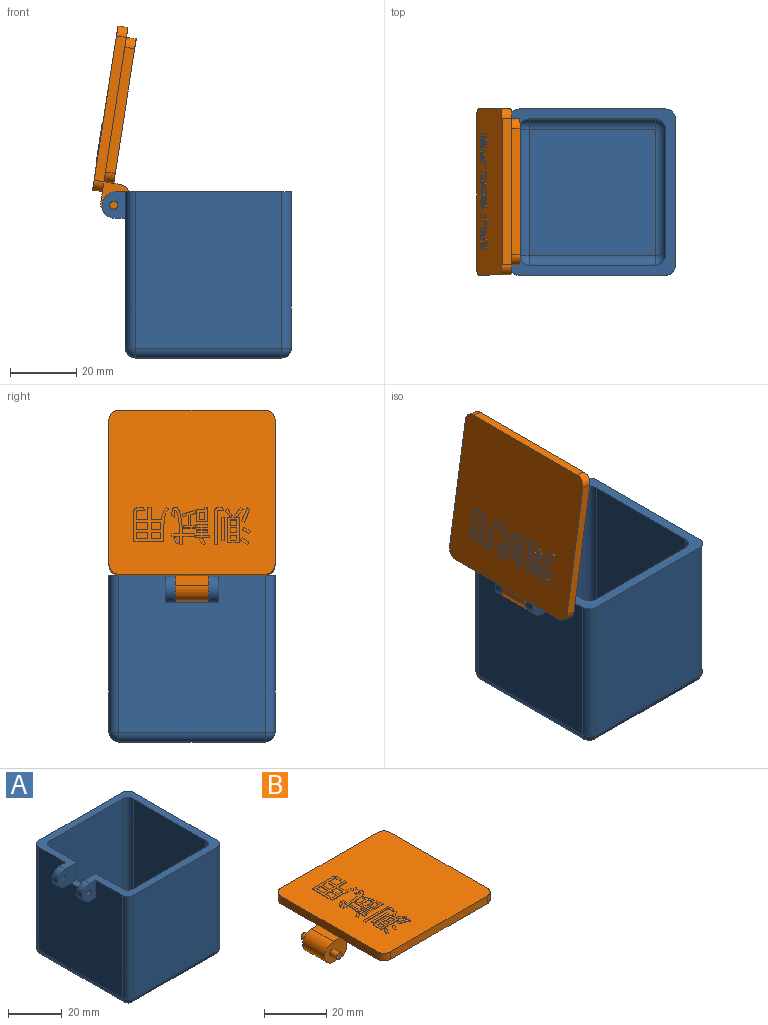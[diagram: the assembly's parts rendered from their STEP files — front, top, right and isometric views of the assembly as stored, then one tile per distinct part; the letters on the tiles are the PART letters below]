
ASSEMBLY  parts=2 mates=1
PART A: 46 faces, bbox 57x50x50 mm
  f0: plane 47x44mm, normal (-1,0,0), area 1940mm2, adj f1,f13,f14,f15,f16,f17,f34,f36
  f1: plane 53x50mm, normal (0,0,1), area 552mm2, adj f0,f2,f3,f4,f5,f7,f8,f9
  f2: plane 44x38mm, normal (1,0,0), area 1592mm2, adj f1,f11,f12,f13,f22,f26,f27
  f3: plane 47x44mm, normal (1,0,0), area 2068mm2, adj f1,f39,f43,f45
  f4: plane 47x44mm, normal (0,1,0), area 2068mm2, adj f1,f36,f42,f45
  f5: plane 47x44mm, normal (0,-1,0), area 2068mm2, adj f1,f34,f38,f39
  f6: plane 44x44mm, normal (0,0,-1), area 1936mm2, adj f37,f38,f42,f43
  f7: plane 44x38mm, normal (-1,0,0), area 1672mm2, adj f1,f24,f30,f33
  f8: plane 44x38mm, normal (0,-1,0), area 1672mm2, adj f1,f27,f31,f33
  f9: plane 44x38mm, normal (0,1,0), area 1672mm2, adj f1,f22,f24,f25
  f10: plane 38x38mm, normal (0,0,1), area 1444mm2, adj f25,f26,f30,f31
  f11: plane 10x8mm, normal (0,-1,0), area 68.2mm2, adj f1,f2,f13,f15,f19,f21
  f12: plane 10x8mm, normal (0,1,0), area 68.2mm2, adj f1,f2,f13,f17,f18,f20
  f13: plane 10x3mm, normal (0,0,1), area 30mm2, adj f0,f2,f11,f12
  f14: plane 8x7mm, normal (0,1,0), area 44.2mm2, adj f0,f1,f15,f19,f21
  f15: plane 3x3mm, normal (0,0,-1), area 9mm2, adj f0,f11,f14,f21
  f16: plane 8x7mm, normal (0,-1,0), area 44.2mm2, adj f0,f1,f17,f18,f20
  f17: plane 3x3mm, normal (0,0,-1), area 9mm2, adj f0,f12,f16,f20
  f18: cylinder r=1.25mm len=3mm, axis (0,-1,0), area 23.6mm2, adj f12,f16
  f19: cylinder r=1.25mm len=3mm, axis (0,-1,0), area 23.6mm2, adj f11,f14
  f20: cylinder r=4mm len=8mm, axis (0,1,0), area 37.7mm2, adj f1,f12,f16,f17
  f21: cylinder r=4mm len=8mm, axis (0,1,0), area 37.7mm2, adj f1,f11,f14,f15
  f22: cylinder r=3mm len=44mm, axis (0,0,1), area 207.3mm2, adj f1,f2,f9,f23
  f23: sphere r=3mm, area 14.1mm2, adj f22,f25,f26
  f24: cylinder r=3mm len=44mm, axis (0,0,-1), area 207.3mm2, adj f1,f7,f9,f28
  f25: cylinder r=3mm len=38mm, axis (1,0,0), area 179.1mm2, adj f9,f10,f23,f28
  f26: cylinder r=3mm len=38mm, axis (0,-1,0), area 179.1mm2, adj f2,f10,f23,f29
  f27: cylinder r=3mm len=44mm, axis (0,0,-1), area 207.3mm2, adj f1,f2,f8,f29
  f28: sphere r=3mm, area 14.1mm2, adj f24,f25,f30
  f29: sphere r=3mm, area 14.1mm2, adj f26,f27,f31
  f30: cylinder r=3mm len=38mm, axis (0,1,0), area 179.1mm2, adj f7,f10,f28,f32
  f31: cylinder r=3mm len=38mm, axis (-1,0,0), area 179.1mm2, adj f8,f10,f29,f32
  f32: sphere r=3mm, area 14.1mm2, adj f30,f31,f33
  f33: cylinder r=3mm len=44mm, axis (0,0,1), area 207.3mm2, adj f1,f7,f8,f32
  f34: cylinder r=3mm len=47mm, axis (0,0,1), area 221.5mm2, adj f0,f1,f5,f35
  f35: sphere r=3mm, area 14.1mm2, adj f34,f37,f38
  f36: cylinder r=3mm len=47mm, axis (0,0,-1), area 221.5mm2, adj f0,f1,f4,f40
  f37: cylinder r=3mm len=44mm, axis (0,-1,0), area 207.3mm2, adj f0,f6,f35,f40
  f38: cylinder r=3mm len=44mm, axis (1,0,0), area 207.3mm2, adj f5,f6,f35,f41
  f39: cylinder r=3mm len=47mm, axis (0,0,-1), area 221.5mm2, adj f1,f3,f5,f41
  f40: sphere r=3mm, area 14.1mm2, adj f36,f37,f42
  f41: sphere r=3mm, area 14.1mm2, adj f38,f39,f43
  f42: cylinder r=3mm len=44mm, axis (-1,0,0), area 207.3mm2, adj f4,f6,f40,f44
  f43: cylinder r=3mm len=44mm, axis (0,1,0), area 207.3mm2, adj f3,f6,f41,f44
  f44: sphere r=3mm, area 14.1mm2, adj f42,f43,f45
  f45: cylinder r=3mm len=47mm, axis (0,0,1), area 221.5mm2, adj f1,f3,f4,f44
PART B: 194 faces, bbox 57x50x11.2 mm
  f0: plane 50x50mm, normal (0,0,1), area 2315.2mm2, adj f2,f3,f4,f5,f27,f28,f29,f30
  f1: plane 14x3mm, normal (-1,0,0), area 42mm2, adj f6,f11,f13,f24
  f2: plane 44x3mm, normal (1,0,0), area 132mm2, adj f0,f6,f27,f30
  f3: plane 44x3mm, normal (0,1,0), area 132mm2, adj f0,f6,f27,f28
  f4: plane 44x3mm, normal (-1,0,0), area 132mm2, adj f0,f6,f16,f28,f29
  f5: plane 44x3mm, normal (0,-1,0), area 132mm2, adj f0,f6,f29,f30
  f6: plane 50x50mm, normal (0,0,-1), area 534mm2, adj f1,f2,f3,f4,f5,f7,f8,f9
  f7: plane 38x3mm, normal (1,0,0), area 114mm2, adj f6,f11,f23,f26
  f8: plane 38x3mm, normal (0,-1,0), area 114mm2, adj f6,f11,f23,f24
  f9: plane 14x3mm, normal (-1,0,0), area 42mm2, adj f6,f11,f14,f25
  f10: plane 38x3mm, normal (0,1,0), area 114mm2, adj f6,f11,f25,f26
  f11: plane 44x44mm, normal (0,0,-1), area 1928.3mm2, adj f1,f7,f8,f9,f10,f12,f23,f24
  f12: plane 10x2mm, normal (1,0,0), area 20mm2, adj f11,f13,f14,f22
  f13: plane 10x8mm, normal (0,-1,0), area 66.7mm2, adj f1,f6,f12,f15,f16,f17,f21,f22
  f14: plane 10x8mm, normal (0,1,0), area 66.7mm2, adj f6,f9,f12,f15,f16,f19,f21,f22
  f15: plane 10x3mm, normal (0,0,-1), area 30mm2, adj f13,f14,f21,f22
  f16: plane 10x3mm, normal (0,0,1), area 30mm2, adj f4,f13,f14,f21
  f17: cylinder r=1.2mm len=3mm, axis (0,1,0), area 22.6mm2, adj f13,f18
  f18: plane 2.4x2.4mm, normal (0,-1,0), area 4.5mm2, adj f17
  f19: cylinder r=1.2mm len=3mm, axis (0,-1,0), area 22.6mm2, adj f14,f20
  f20: plane 2.4x2.4mm, normal (0,1,0), area 4.5mm2, adj f19
  f21: cylinder r=4mm len=10mm, axis (0,-1,0), area 125.7mm2, adj f13,f14,f15,f16
  f22: cylinder r=3mm len=10mm, axis (0,1,0), area 47.1mm2, adj f12,f13,f14,f15
  f23: cylinder r=3mm len=3mm, axis (0,0,-1), area 14.1mm2, adj f6,f7,f8,f11
  f24: cylinder r=3mm len=3mm, axis (0,0,1), area 14.1mm2, adj f1,f6,f8,f11
  f25: cylinder r=3mm len=3mm, axis (0,0,-1), area 14.1mm2, adj f6,f9,f10,f11
  f26: cylinder r=3mm len=3mm, axis (0,0,1), area 14.1mm2, adj f6,f7,f10,f11
  f27: cylinder r=3mm len=3mm, axis (0,0,-1), area 14.1mm2, adj f0,f2,f3,f6
  f28: cylinder r=3mm len=3mm, axis (0,0,1), area 14.1mm2, adj f0,f3,f4,f6
  f29: cylinder r=3mm len=3mm, axis (0,0,-1), area 14.1mm2, adj f0,f4,f5,f6
  f30: cylinder r=3mm len=3mm, axis (0,0,1), area 14.1mm2, adj f0,f2,f5,f6
  f31: plane 1.52x0.2mm, normal (0,1,0), area 0.3mm2, adj f32,f46,f47,f48
  f32: plane 1.95x0.2mm, normal (1,0,0), area 0.4mm2, adj f31,f33,f47,f48
  f33: plane 1.52x0.2mm, normal (0,-1,0), area 0.3mm2, adj f32,f46,f47,f48
  f34: plane 1.55x0.2mm, normal (0,1,0), area 0.3mm2, adj f35,f43,f47,f49
  f35: plane 1.95x0.2mm, normal (1,0,0), area 0.4mm2, adj f34,f36,f47,f49
  f36: plane 1.55x0.2mm, normal (0,-1,0), area 0.3mm2, adj f35,f43,f47,f49
  f37: plane 1.51x0.2mm, normal (0,1,0), area 0.3mm2, adj f38,f44,f47,f50
  f38: plane 1.95x0.2mm, normal (1,0,0), area 0.4mm2, adj f37,f39,f47,f50
  f39: plane 1.51x0.2mm, normal (0,-1,0), area 0.3mm2, adj f38,f44,f47,f50
  f40: plane 3.57x0.2mm, normal (-1,0,0), area 0.7mm2, adj f0,f41,f45,f47
  f41: plane 7.73x0.2mm, normal (0,-1,0), area 1.5mm2, adj f0,f40,f42,f47
  f42: plane 3.57x0.2mm, normal (1,0,0), area 0.7mm2, adj f0,f41,f45,f47
  f43: plane 1.95x0.2mm, normal (-1,0,0), area 0.4mm2, adj f34,f36,f47,f49
  f44: plane 1.95x0.2mm, normal (-1,0,0), area 0.4mm2, adj f37,f39,f47,f50
  f45: plane 7.73x0.2mm, normal (0,1,0), area 1.5mm2, adj f0,f40,f42,f47
  f46: plane 1.95x0.2mm, normal (-1,0,0), area 0.4mm2, adj f31,f33,f47,f48
  f47: plane 7.73x3.57mm, normal (0,0,1), area 18.7mm2, adj f31,f32,f33,f34,f35,f36,f37,f38
  f48: plane 1.95x1.52mm, normal (0,0,1), area 3mm2, adj f31,f32,f33,f46
  f49: plane 1.95x1.55mm, normal (0,0,1), area 3mm2, adj f34,f35,f36,f43
  f50: plane 1.95x1.51mm, normal (0,0,1), area 2.9mm2, adj f37,f38,f39,f44
  f51: plane 0.69x0.38mm, normal (-0.87,-0.49,0), area 0.2mm2, adj f0,f52,f54,f55
  f52: extruded ~1.97x1.37mm, area 0.5mm2, adj f0,f51,f53,f55
  f53: plane 0.73x0.46mm, normal (0.85,0.53,0), area 0.2mm2, adj f0,f52,f54,f55
  f54: extruded ~1.89x1.41mm, area 0.5mm2, adj f0,f51,f53,f55
  f55: plane 2.35x2.1mm, normal (0,0,1), area 2mm2, adj f51,f52,f53,f54
  f56: plane 0.85x0.22mm, normal (-0.97,0.25,0), area 0.2mm2, adj f0,f57,f59,f60
  f57: extruded ~2.27x1.64mm, area 0.6mm2, adj f0,f56,f58,f60
  f58: extruded ~0.72x0.51mm, area 0.2mm2, adj f0,f57,f59,f60
  f59: extruded ~2.56x1.78mm, area 0.6mm2, adj f0,f56,f58,f60
  f60: plane 2.78x2.5mm, normal (0,0,1), area 2.5mm2, adj f56,f57,f58,f59
  f61: plane 0.83x0.2mm, normal (-1,0,0), area 0.2mm2, adj f0,f62,f68,f69
  f62: plane 10.14x0.2mm, normal (0,-1,0), area 2mm2, adj f0,f61,f63,f69
  f63: extruded ~0.3x0.27mm, area 0.1mm2, adj f0,f62,f64,f69
  f64: extruded ~1.57x0.2mm, area 0.3mm2, adj f0,f63,f65,f69
  f65: extruded ~0.87x0.27mm, area 0.2mm2, adj f0,f64,f66,f69
  f66: extruded ~1.94x0.2mm, area 0.4mm2, adj f0,f65,f67,f69
  f67: extruded ~0.98x0.48mm, area 0.2mm2, adj f0,f66,f68,f69
  f68: plane 10.13x0.2mm, normal (0,1,0), area 2mm2, adj f0,f61,f67,f69
  f69: plane 11.28x2.7mm, normal (0,0,1), area 10.6mm2, adj f61,f62,f63,f64,f65,f66,f67,f68
  f70: plane 0.82x0.2mm, normal (-1,0,0), area 0.2mm2, adj f0,f71,f73,f74
  f71: plane 7.03x0.2mm, normal (0,-1,0), area 1.4mm2, adj f0,f70,f72,f74
  f72: plane 0.82x0.2mm, normal (1,0,0), area 0.2mm2, adj f0,f71,f73,f74
  f73: plane 7.03x0.2mm, normal (0,1,0), area 1.4mm2, adj f0,f70,f72,f74
  f74: plane 7.03x0.82mm, normal (0,0,1), area 5.7mm2, adj f70,f71,f72,f73
  f75: plane 0.66x0.53mm, normal (-0.63,-0.78,0), area 0.2mm2, adj f0,f76,f78,f79
  f76: extruded ~1.94x1.32mm, area 0.5mm2, adj f0,f75,f77,f79
  f77: plane 0.73x0.55mm, normal (0.6,0.8,0), area 0.2mm2, adj f0,f76,f78,f79
  f78: extruded ~1.95x1.25mm, area 0.5mm2, adj f0,f75,f77,f79
  f79: plane 2.48x1.98mm, normal (0,0,1), area 2mm2, adj f75,f76,f77,f78
  f80: plane 0.67x0.52mm, normal (-0.61,-0.79,0), area 0.2mm2, adj f0,f81,f83,f84
  f81: extruded ~2.03x1.22mm, area 0.5mm2, adj f0,f80,f82,f84
  f82: plane 0.75x0.52mm, normal (0.57,0.82,0), area 0.2mm2, adj f0,f81,f83,f84
  f83: extruded ~2.03x1.14mm, area 0.5mm2, adj f0,f80,f82,f84
  f84: plane 2.55x1.89mm, normal (0,0,1), area 2.1mm2, adj f80,f81,f82,f83
  f85: extruded ~3.92x1.71mm, area 0.9mm2, adj f0,f86,f88,f89
  f86: plane 0.83x0.49mm, normal (0.86,-0.51,0), area 0.2mm2, adj f0,f85,f87,f89
  f87: extruded ~3.93x1.61mm, area 0.9mm2, adj f0,f86,f88,f89
  f88: plane 0.73x0.48mm, normal (-0.84,0.55,0), area 0.2mm2, adj f0,f85,f87,f89
  f89: plane 4.41x2.44mm, normal (0,0,1), area 3.8mm2, adj f85,f86,f87,f88
  f90: plane 0.67x0.43mm, normal (0.84,0.54,0), area 0.2mm2, adj f0,f91,f93,f94
  f91: extruded ~1.52x1.11mm, area 0.4mm2, adj f0,f90,f92,f94
  f92: plane 0.64x0.36mm, normal (-0.87,-0.49,0), area 0.1mm2, adj f0,f91,f93,f94
  f93: extruded ~1.59x1.09mm, area 0.4mm2, adj f0,f90,f92,f94
  f94: plane 1.95x1.76mm, normal (0,0,1), area 1.5mm2, adj f90,f91,f92,f93
  f95: plane 0.73x0.43mm, normal (0.86,0.51,0), area 0.2mm2, adj f0,f96,f98,f99
  f96: extruded ~1.58x0.93mm, area 0.4mm2, adj f0,f95,f97,f99
  f97: plane 0.72x0.36mm, normal (-0.89,-0.45,0), area 0.2mm2, adj f0,f96,f98,f99
  f98: extruded ~1.66x0.91mm, area 0.4mm2, adj f0,f95,f97,f99
  f99: plane 2.02x1.64mm, normal (0,0,1), area 1.5mm2, adj f95,f96,f97,f98
  f100: plane 1.72x0.2mm, normal (1,0,0), area 0.3mm2, adj f101,f109,f110,f111
  f101: plane 2.04x0.2mm, normal (0,-1,0), area 0.4mm2, adj f100,f102,f110,f111
  f102: plane 1.72x0.2mm, normal (-1,0,0), area 0.3mm2, adj f101,f109,f110,f111
  f103: plane 3.57x0.2mm, normal (0,1,0), area 0.7mm2, adj f0,f104,f108,f110
  f104: plane 3.31x0.2mm, normal (-1,0,0), area 0.7mm2, adj f0,f103,f105,f110
  f105: plane 4.15x0.2mm, normal (0,-1,0), area 0.8mm2, adj f0,f104,f106,f110
  f106: plane 0.79x0.2mm, normal (1,0,0), area 0.2mm2, adj f0,f105,f107,f110
  f107: plane 0.58x0.2mm, normal (0,1,0), area 0.1mm2, adj f0,f106,f108,f110
  f108: plane 2.52x0.2mm, normal (1,0,0), area 0.5mm2, adj f0,f103,f107,f110
  f109: plane 2.04x0.2mm, normal (0,1,0), area 0.4mm2, adj f100,f102,f110,f111
  f110: plane 4.15x3.31mm, normal (0,0,1), area 8.8mm2, adj f100,f101,f102,f103,f104,f105,f106,f107
  f111: plane 2.04x1.72mm, normal (0,0,1), area 3.5mm2, adj f100,f101,f102,f109
  f112: plane 0.73x0.2mm, normal (0,-1,0), area 0.1mm2, adj f0,f113,f115,f116
  f113: plane 3.28x0.2mm, normal (1,0,0), area 0.7mm2, adj f0,f112,f114,f116
  f114: plane 0.73x0.2mm, normal (0,1,0), area 0.1mm2, adj f0,f113,f115,f116
  f115: plane 3.28x0.2mm, normal (-1,0,0), area 0.7mm2, adj f0,f112,f114,f116
  f116: plane 3.28x0.73mm, normal (0,0,1), area 2.4mm2, adj f112,f113,f114,f115
  f117: plane 0.73x0.2mm, normal (0,1,0), area 0.1mm2, adj f0,f118,f120,f121
  f118: plane 3.28x0.2mm, normal (-1,0,0), area 0.7mm2, adj f0,f117,f119,f121
  f119: plane 0.73x0.2mm, normal (0,-1,0), area 0.1mm2, adj f0,f118,f120,f121
  f120: plane 3.28x0.2mm, normal (1,0,0), area 0.7mm2, adj f0,f117,f119,f121
  f121: plane 3.28x0.73mm, normal (0,0,1), area 2.4mm2, adj f117,f118,f119,f120
  f122: plane 0.76x0.2mm, normal (0,-1,0), area 0.2mm2, adj f0,f123,f125,f126
  f123: plane 4.03x0.2mm, normal (1,0,0), area 0.8mm2, adj f0,f122,f124,f126
  f124: plane 0.76x0.2mm, normal (0,1,0), area 0.2mm2, adj f0,f123,f125,f126
  f125: plane 4.03x0.2mm, normal (-1,0,0), area 0.8mm2, adj f0,f122,f124,f126
  f126: plane 4.03x0.76mm, normal (0,0,1), area 3mm2, adj f122,f123,f124,f125
  f127: plane 3.05x0.2mm, normal (0,1,0), area 0.6mm2, adj f0,f128,f138,f139
  f128: plane 1.32x0.2mm, normal (1,0,0), area 0.3mm2, adj f0,f127,f129,f139
  f129: plane 0.83x0.2mm, normal (0,1,0), area 0.2mm2, adj f0,f128,f130,f139
  f130: plane 3.46x0.2mm, normal (-1,0,0), area 0.7mm2, adj f0,f129,f131,f139
  f131: plane 0.83x0.2mm, normal (0,-1,0), area 0.2mm2, adj f0,f130,f132,f139
  f132: plane 1.3x0.2mm, normal (1,0,0), area 0.3mm2, adj f0,f131,f133,f139
  f133: plane 3.26x0.2mm, normal (0,-1,0), area 0.7mm2, adj f0,f132,f134,f139
  f134: extruded ~1.5x0.36mm, area 0.3mm2, adj f0,f133,f135,f139
  f135: plane 0.89x0.26mm, normal (0.28,-0.96,0), area 0.2mm2, adj f0,f134,f136,f139
  f136: extruded ~3.9x1.14mm, area 0.8mm2, adj f0,f135,f137,f139
  f137: plane 0.78x0.2mm, normal (-0.11,0.99,0), area 0.2mm2, adj f0,f136,f138,f139
  f138: extruded ~1.73x0.46mm, area 0.4mm2, adj f0,f127,f137,f139
  f139: plane 5.34x4.15mm, normal (0,0,1), area 9mm2, adj f127,f128,f129,f130,f131,f132,f133,f134
  f140: plane 2.37x0.2mm, normal (1,0,0), area 0.5mm2, adj f0,f141,f153,f154
  f141: plane 0.87x0.2mm, normal (0,1,0), area 0.2mm2, adj f0,f140,f142,f154
  f142: plane 2.4x0.2mm, normal (-1,0,0), area 0.5mm2, adj f0,f141,f143,f154
  f143: extruded ~2.39x0.2mm, area 0.5mm2, adj f0,f142,f144,f154
  f144: plane 0.9x0.2mm, normal (-1,0,0), area 0.2mm2, adj f0,f143,f145,f154
  f145: extruded ~2.39x0.2mm, area 0.5mm2, adj f0,f144,f146,f154
  f146: plane 3.61x0.2mm, normal (-1,0,0), area 0.7mm2, adj f0,f145,f147,f154
  f147: plane 0.87x0.2mm, normal (0,-1,0), area 0.2mm2, adj f0,f146,f148,f154
  f148: plane 3.65x0.2mm, normal (1,0,0), area 0.7mm2, adj f0,f147,f149,f154
  f149: extruded ~8.02x2.15mm, area 1.7mm2, adj f0,f148,f150,f154
  f150: extruded ~2.42x1.15mm, area 0.6mm2, adj f0,f149,f151,f154
  f151: extruded ~0.69x0.49mm, area 0.2mm2, adj f0,f150,f152,f154
  f152: extruded ~2.02x0.33mm, area 0.4mm2, adj f0,f151,f153,f154
  f153: extruded ~7.12x1.41mm, area 1.5mm2, adj f0,f140,f152,f154
  f154: plane 11.28x6.95mm, normal (0,0,1), area 16.9mm2, adj f140,f141,f142,f143,f144,f145,f146,f147
  f155: plane 3.33x0.2mm, normal (-1,0,0), area 0.7mm2, adj f156,f188,f189,f193
  f156: plane 2.05x0.2mm, normal (0,1,0), area 0.4mm2, adj f155,f157,f189,f193
  f157: plane 3.33x0.2mm, normal (1,0,0), area 0.7mm2, adj f156,f188,f189,f193
  f158: plane 3x0.2mm, normal (-1,0,0), area 0.6mm2, adj f159,f184,f189,f192
  f159: extruded ~1.32x0.2mm, area 0.3mm2, adj f158,f160,f189,f192
  f160: plane 0.73x0.2mm, normal (0,1,0), area 0.1mm2, adj f159,f161,f189,f192
  f161: plane 2.95x0.2mm, normal (1,0,0), area 0.6mm2, adj f160,f184,f189,f192
  f162: plane 2.95x0.2mm, normal (1,0,0), area 0.6mm2, adj f163,f185,f189,f191
  f163: plane 1.98x0.2mm, normal (0,-1,0), area 0.4mm2, adj f162,f164,f189,f191
  f164: plane 2.95x0.2mm, normal (-1,0,0), area 0.6mm2, adj f163,f185,f189,f191
  f165: plane 1.98x0.2mm, normal (0,-1,0), area 0.4mm2, adj f166,f186,f189,f190
  f166: plane 3.33x0.2mm, normal (-1,0,0), area 0.7mm2, adj f165,f167,f189,f190
  f167: plane 1.98x0.2mm, normal (0,1,0), area 0.4mm2, adj f166,f186,f189,f190
  f168: plane 9.17x0.2mm, normal (0,1,0), area 1.8mm2, adj f0,f169,f187,f189
  f169: plane 9x0.2mm, normal (-1,0,0), area 1.8mm2, adj f0,f168,f170,f189
  f170: plane 4.45x0.2mm, normal (0,-1,0), area 0.9mm2, adj f0,f169,f171,f189
  f171: extruded ~5.43x1.48mm, area 1.2mm2, adj f0,f170,f172,f189
  f172: extruded ~0.71x0.61mm, area 0.2mm2, adj f0,f171,f173,f189
  f173: extruded ~3.83x1.55mm, area 0.8mm2, adj f0,f172,f174,f189
  f174: plane 3.09x0.2mm, normal (1,0,0), area 0.6mm2, adj f0,f173,f175,f189
  f175: plane 3.65x0.2mm, normal (0,-1,0), area 0.7mm2, adj f0,f174,f176,f189
  f176: plane 0.92x0.2mm, normal (1,0,0), area 0.2mm2, adj f0,f175,f177,f189
  f177: plane 3.65x0.2mm, normal (0,1,0), area 0.7mm2, adj f0,f176,f178,f189
  f178: plane 3.33x0.2mm, normal (1,0,0), area 0.7mm2, adj f0,f177,f179,f189
  f179: plane 2.51x0.2mm, normal (0,-1,0), area 0.5mm2, adj f0,f178,f180,f189
  f180: extruded ~0.33x0.32mm, area 0.1mm2, adj f0,f179,f181,f189
  f181: extruded ~1.93x0.2mm, area 0.4mm2, adj f0,f180,f182,f189
  f182: extruded ~0.89x0.31mm, area 0.2mm2, adj f0,f181,f183,f189
  f183: extruded ~2.3x0.2mm, area 0.5mm2, adj f0,f182,f187,f189
  f184: plane 2.05x0.2mm, normal (0,-1,0), area 0.4mm2, adj f158,f161,f189,f192
  f185: plane 1.98x0.2mm, normal (0,1,0), area 0.4mm2, adj f162,f164,f189,f191
  f186: plane 3.33x0.2mm, normal (1,0,0), area 0.7mm2, adj f165,f167,f189,f190
  f187: extruded ~1.03x0.56mm, area 0.3mm2, adj f0,f168,f183,f189
  f188: plane 2.05x0.2mm, normal (0,-1,0), area 0.4mm2, adj f155,f157,f189,f193
  f189: plane 10.49x10.49mm, normal (0,0,1), area 46.4mm2, adj f155,f156,f157,f158,f159,f160,f161,f162
  f190: plane 3.33x1.98mm, normal (0,0,1), area 6.6mm2, adj f165,f166,f167,f186
  f191: plane 2.95x1.98mm, normal (0,0,1), area 5.8mm2, adj f162,f163,f164,f185
  f192: plane 3x2.05mm, normal (0,0,1), area 6.1mm2, adj f158,f159,f160,f161,f184
  f193: plane 3.33x2.05mm, normal (0,0,1), area 6.8mm2, adj f155,f156,f157,f188
PLACE A t=(-2.21,7.26,-12.2)mm fixed
PLACE B rot(axis=(0,-1,0),81.2deg) t=(-33.26,7.26,63.04)mm
MATE revolute B.f17 <-> A.f18  axis (0,-1,0) through (-30.71,-0.74,33.8)mm
